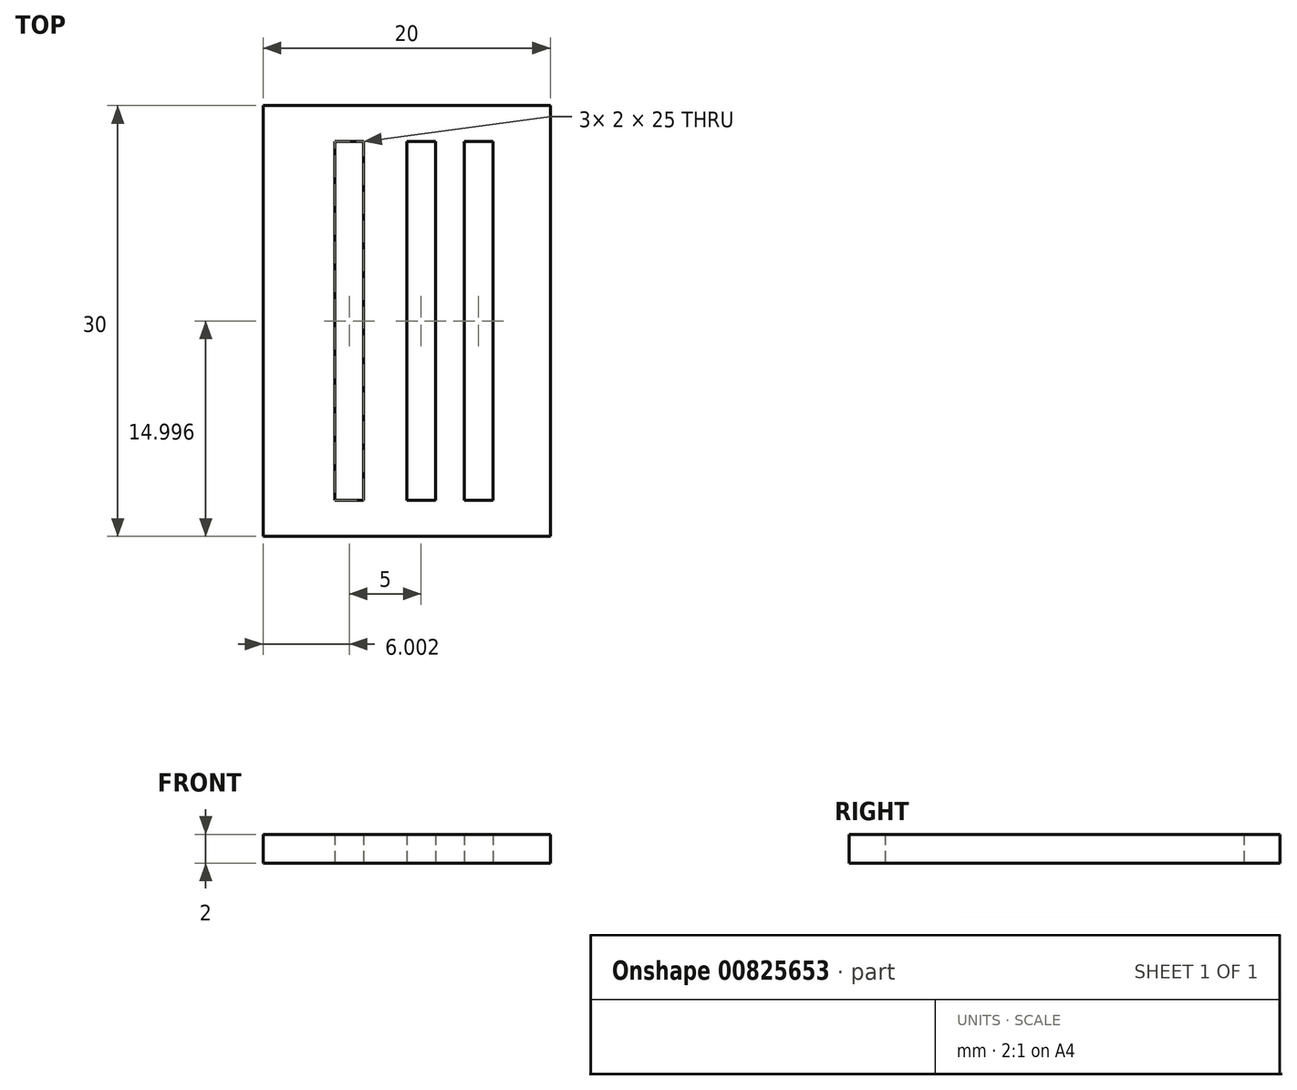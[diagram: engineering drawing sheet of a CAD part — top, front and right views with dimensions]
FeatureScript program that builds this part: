
annotation { "Feature Type Name" : "Feature", "Feature Type Description" : "" }
export const myFeature = defineFeature(function(context is Context, id is Id, definition is map)
    precondition{}
    {
        {
            var Q0;
            Q0=qCreatedBy(makeId("Top.planeOp"),FACE);
            var sketch = newSketch(context, id + "F0", { "sketchPlane" : qUnion([Q0])});
            skLineSegment(sketch, "E0.bottom", {"start": v(-26.36, 15.18) * mm, "end": v(-6.36, 15.18) * mm});
            skLineSegment(sketch, "E0.top", {"start": v(-26.36, -14.82) * mm, "end": v(-6.36, -14.82) * mm});
            skLineSegment(sketch, "E0.left", {"start": v(-26.36, 15.18) * mm, "end": v(-26.36, -14.82) * mm});
            skLineSegment(sketch, "E0.right", {"start": v(-6.36, 15.18) * mm, "end": v(-6.36, -14.82) * mm});
            skLineSegment(sketch, "E1", {"start": v(-26.36, -14.82) * mm, "end": v(-26.36, -12.32) * mm});
            skLineSegment(sketch, "E2", {"start": v(-26.36, -12.32) * mm, "end": v(-21.36, -12.32) * mm});
            skLineSegment(sketch, "E3", {"start": v(-21.36, -12.32) * mm, "end": v(-21.36, 12.68) * mm});
            skLineSegment(sketch, "E4", {"start": v(-21.36, 12.68) * mm, "end": v(-19.36, 12.68) * mm});
            skLineSegment(sketch, "E5", {"start": v(-19.36, 12.68) * mm, "end": v(-19.36, -12.32) * mm});
            skLineSegment(sketch, "E6", {"start": v(-19.36, -12.32) * mm, "end": v(-21.36, -12.32) * mm});
            skLineSegment(sketch, "E7", {"start": v(-19.36, -12.32) * mm, "end": v(-16.36, -12.32) * mm});
            skLineSegment(sketch, "E8", {"start": v(-16.36, -12.32) * mm, "end": v(-14.36, -12.32) * mm});
            skLineSegment(sketch, "E9", {"start": v(-14.36, -12.32) * mm, "end": v(-14.36, 12.68) * mm});
            skLineSegment(sketch, "E10", {"start": v(-14.36, 12.68) * mm, "end": v(-16.36, 12.68) * mm});
            skLineSegment(sketch, "E11", {"start": v(-16.36, 12.68) * mm, "end": v(-16.36, -12.32) * mm});
            skLineSegment(sketch, "E12", {"start": v(-14.36, -12.32) * mm, "end": v(-12.36, -12.32) * mm});
            skLineSegment(sketch, "E13", {"start": v(-12.36, -12.32) * mm, "end": v(-12.36, 12.68) * mm});
            skLineSegment(sketch, "E14", {"start": v(-12.36, 12.68) * mm, "end": v(-10.36, 12.68) * mm});
            skLineSegment(sketch, "E15", {"start": v(-10.36, 12.68) * mm, "end": v(-10.36, -12.32) * mm});
            skLineSegment(sketch, "E16", {"start": v(-10.36, -12.32) * mm, "end": v(-12.36, -12.32) * mm});
            skSolve(sketch);
        }
        {
            var Q0;
            Q0=makeQuery(id+"F0.imprint","IMPRINT",FACE,{"disambiguationData":[TD([[makeQuery(id+"F0.imprint","IMPRINT",EDGE,{"derivedFrom":sQuery(id+"F0.wireOp",EDGE,"E0.bottom")}),-1.0]])]});
            extrude(context, id + "F1", {"entities" : qUnion([Q0]), "depth" : 2 * mm, "offsetDistance" : 25.4 * mm});
        }
    });
